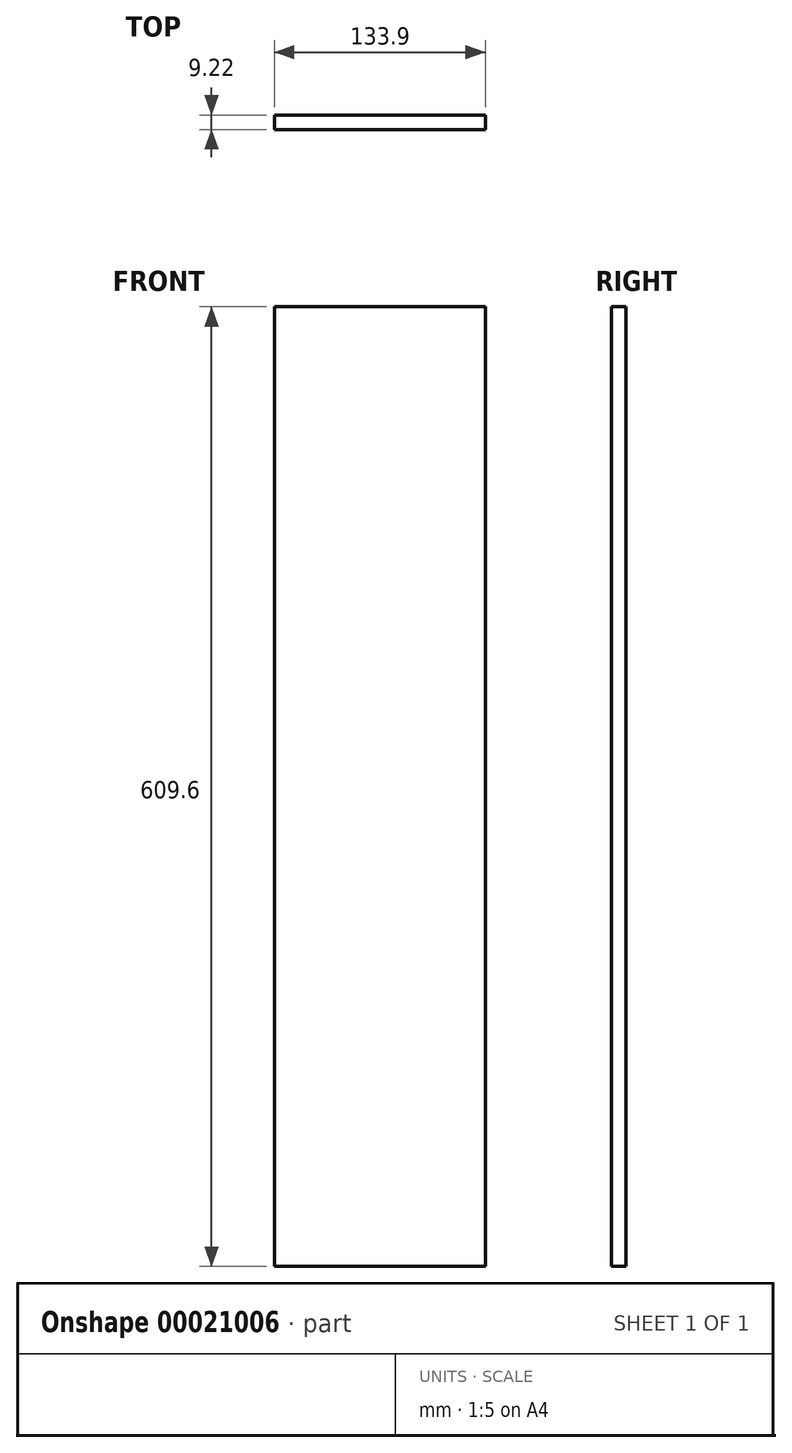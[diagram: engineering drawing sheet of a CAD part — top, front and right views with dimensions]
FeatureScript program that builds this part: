
annotation { "Feature Type Name" : "Feature", "Feature Type Description" : "" }
export const myFeature = defineFeature(function(context is Context, id is Id, definition is map)
    precondition{}
    {
        {
            var Q0;
            Q0=qCreatedBy(makeId("Top.planeOp"),FACE);
            var sketch = newSketch(context, id + "F0", { "sketchPlane" : qUnion([Q0])});
            skLineSegment(sketch, "E0.bottom", {"start": v(-76.07, 75.98) * mm, "end": v(-66.66, 75.98) * mm});
            skLineSegment(sketch, "E0.top", {"start": v(-76.07, -75.98) * mm, "end": v(-66.66, -75.98) * mm});
            skLineSegment(sketch, "E0.left", {"start": v(-76.07, 75.98) * mm, "end": v(-76.07, -75.98) * mm});
            skLineSegment(sketch, "E0.right", {"start": v(-66.66, 75.98) * mm, "end": v(-66.66, -75.98) * mm});
            skLineSegment(sketch, "E1.bottom", {"start": v(-76.07, 75.98) * mm, "end": v(75.5, 75.98) * mm});
            skLineSegment(sketch, "E1.top", {"start": v(-76.07, 66.76) * mm, "end": v(75.5, 66.76) * mm});
            skLineSegment(sketch, "E1.left", {"start": v(-76.07, 75.98) * mm, "end": v(-76.07, 66.76) * mm});
            skLineSegment(sketch, "E1.right", {"start": v(75.5, 75.98) * mm, "end": v(75.5, 66.76) * mm});
            skLineSegment(sketch, "E2.bottom", {"start": v(75.5, 75.98) * mm, "end": v(67.24, 75.98) * mm});
            skLineSegment(sketch, "E2.top", {"start": v(75.5, -75.98) * mm, "end": v(67.24, -75.98) * mm});
            skLineSegment(sketch, "E2.left", {"start": v(75.5, 75.98) * mm, "end": v(75.5, -75.98) * mm});
            skLineSegment(sketch, "E2.right", {"start": v(67.24, 75.98) * mm, "end": v(67.24, -75.98) * mm});
            skLineSegment(sketch, "E3.bottom", {"start": v(75.5, -75.98) * mm, "end": v(-76.07, -75.98) * mm});
            skLineSegment(sketch, "E3.top", {"start": v(75.5, -69.25) * mm, "end": v(-76.07, -69.25) * mm});
            skLineSegment(sketch, "E3.left", {"start": v(75.5, -75.98) * mm, "end": v(75.5, -69.25) * mm});
            skLineSegment(sketch, "E3.right", {"start": v(-76.07, -75.98) * mm, "end": v(-76.07, -69.25) * mm});
            skSolve(sketch);
        }
        {
            var Q0;
            {var subQ3=sQuery(id+"F0.wireOp",EDGE,"E1.bottom");var subQ5=sQuery(id+"F0.wireOp",EDGE,"E0.right");var subQ7=makeQuery(id+"F0.imprint","INTERSECT",VERTEX,{"derivedFrom":[subQ5,subQ3]});Q0=makeQuery(id+"F0.imprint","IMPRINT",FACE,{"disambiguationData":[TD([[makeQuery(id+"F0.imprint","IMPRINT",EDGE,{"disambiguationData":[TD([[subQ7,-1.0]])],"derivedFrom":subQ5}),1.0]])]});}
            extrude(context, id + "F1", {"entities" : qUnion([Q0]), "depth" : 609.6 * mm});
        }
    });
